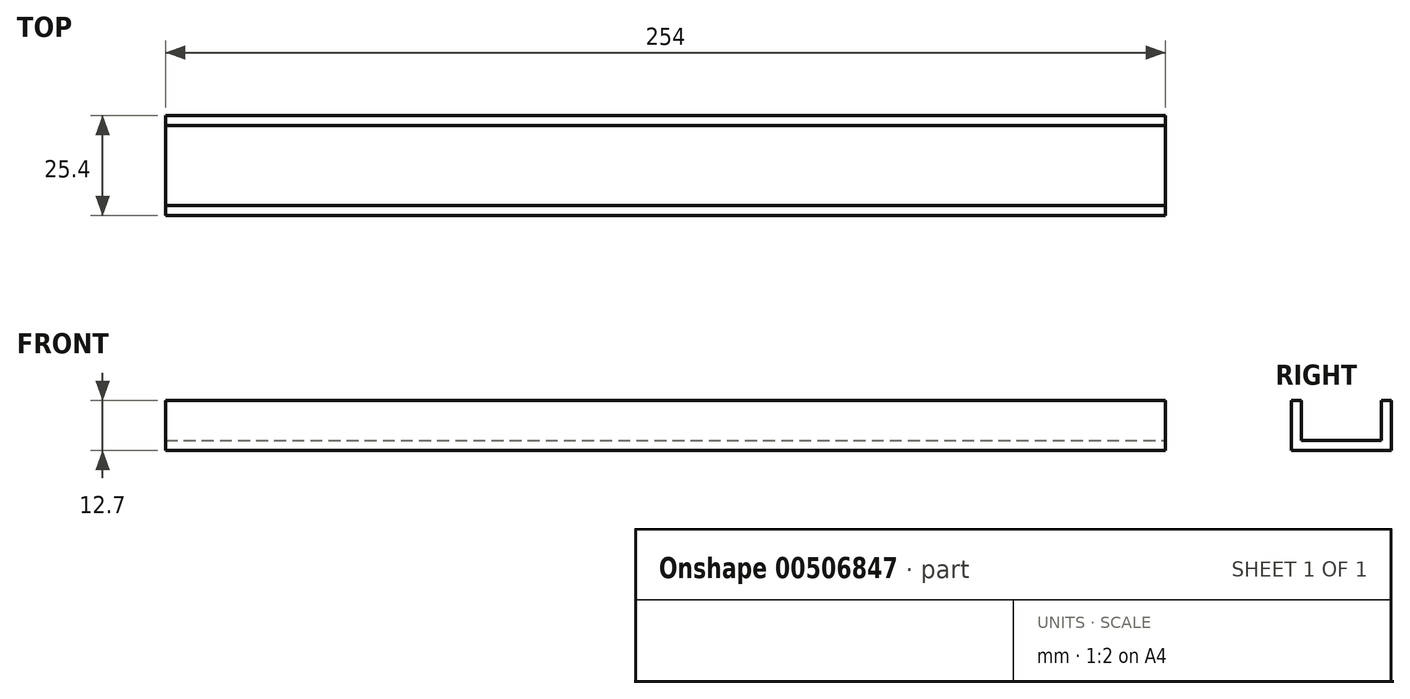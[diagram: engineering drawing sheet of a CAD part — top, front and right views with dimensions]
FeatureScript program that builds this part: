
annotation { "Feature Type Name" : "Feature", "Feature Type Description" : "" }
export const myFeature = defineFeature(function(context is Context, id is Id, definition is map)
    precondition{}
    {
        {
            var Q0;
            Q0=qCreatedBy(makeId("Top.planeOp"),FACE);
            var sketch = newSketch(context, id + "F0", { "sketchPlane" : qUnion([Q0])});
            skLineSegment(sketch, "E0.bottom", {"start": v(-116.38, -4.3) * mm, "end": v(137.62, -4.3) * mm});
            skLineSegment(sketch, "E0.top", {"start": v(-116.38, -29.7) * mm, "end": v(137.62, -29.7) * mm});
            skLineSegment(sketch, "E0.left", {"start": v(-116.38, -4.3) * mm, "end": v(-116.38, -29.7) * mm});
            skLineSegment(sketch, "E0.right", {"start": v(137.62, -4.3) * mm, "end": v(137.62, -29.7) * mm});
            skSolve(sketch);
        }
        {
            var Q0;
            Q0=makeQuery(id+"F0.imprint","IMPRINT",FACE,{"disambiguationData":[TD([[makeQuery(id+"F0.imprint","IMPRINT",EDGE,{"derivedFrom":sQuery(id+"F0.wireOp",EDGE,"E0.bottom")}),-1.0]])]});
            extrude(context, id + "F1", {"entities" : qUnion([Q0]), "depth" : 12.7 * mm, "offsetDistance" : 25.4 * mm});
        }
        {
            var Q0;
            Q0=makeQuery(id+"F1.opExtrude","CAP_FACE",FACE,{"disambiguationData":[OSD([sQuery(id+"F0.wireOp",EDGE,"E0.bottom"),sQuery(id+"F0.wireOp",EDGE,"E0.top"),sQuery(id+"F0.wireOp",EDGE,"E0.left"),sQuery(id+"F0.wireOp",EDGE,"E0.right")])],"isStart":false});
            var Q1;
            Q1=makeQuery(id+"F1.opExtrude","SWEPT_FACE",FACE,{"disambiguationData":[OSD([sQuery(id+"F0.wireOp",EDGE,"E0.right")])]});
            var Q2;
            Q2=makeQuery(id+"F1.opExtrude","SWEPT_FACE",FACE,{"disambiguationData":[OSD([sQuery(id+"F0.wireOp",EDGE,"E0.left")])]});
            shell(context, id + "F2", {"entities" : qUnion([Q0, Q1, Q2]), "thickness" : 2.54 * mm});
        }
    });
